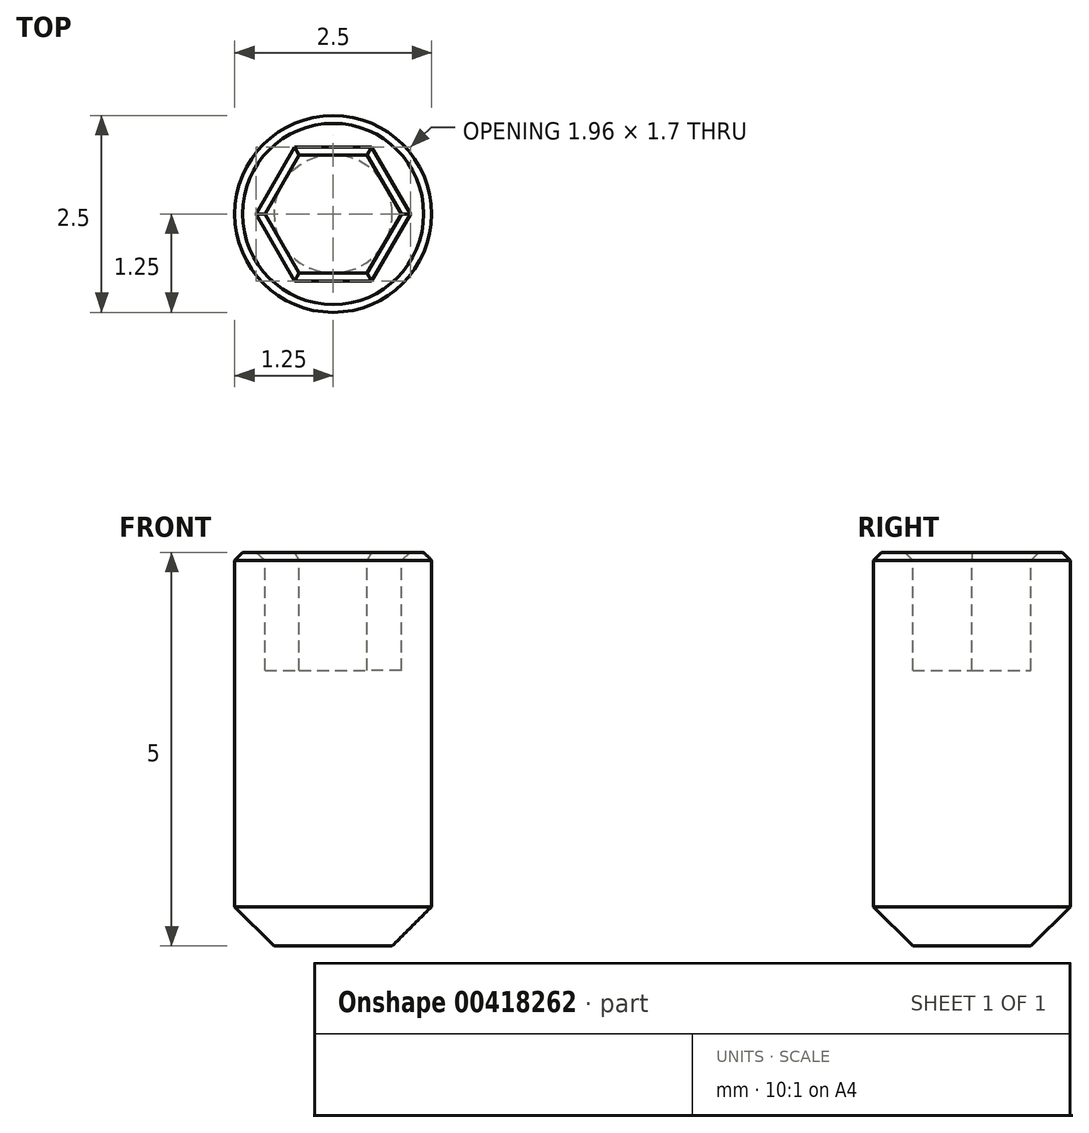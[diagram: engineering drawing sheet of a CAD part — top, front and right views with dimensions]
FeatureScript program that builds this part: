
annotation { "Feature Type Name" : "Feature", "Feature Type Description" : "" }
export const myFeature = defineFeature(function(context is Context, id is Id, definition is map)
    precondition{}
    {
        {
            var Q0;
            Q0=qCreatedBy(makeId("Top.planeOp"),FACE);
            var sketch = newSketch(context, id + "F0", { "sketchPlane" : qUnion([Q0])});
            skCircle(sketch, "E0", {"center": v(0, 0) * mm, "radius": 1.25 * mm});
            skCircle(sketch, "E1.cCircle", {"center": v(0, 0) * mm, "radius": 0.75 * mm, "construction": true});
            skLineSegment(sketch, "E1.0", {"start": v(-0.43, 0.75) * mm, "end": v(0.43, 0.75) * mm});
            skLineSegment(sketch, "E1.1", {"start": v(0.43, 0.75) * mm, "end": v(0.87, 0) * mm});
            skLineSegment(sketch, "E1.2", {"start": v(0.87, 0) * mm, "end": v(0.43, -0.75) * mm});
            skLineSegment(sketch, "E1.3", {"start": v(0.43, -0.75) * mm, "end": v(-0.43, -0.75) * mm});
            skLineSegment(sketch, "E1.4", {"start": v(-0.43, -0.75) * mm, "end": v(-0.87, 0) * mm});
            skLineSegment(sketch, "E1.5", {"start": v(-0.87, 0) * mm, "end": v(-0.43, 0.75) * mm});
            skPoint(sketch, "E1.0.midPoint", {"position": v(0, 0.75) * mm});
            skSolve(sketch);
        }
        {
            var Q0;
            Q0=makeQuery(id+"F0.imprint","IMPRINT",FACE,{"disambiguationData":[TD([[makeQuery(id+"F0.imprint","IMPRINT",EDGE,{"derivedFrom":sQuery(id+"F0.wireOp",EDGE,"E0")}),1.0]])]});
            var Q1;
            Q1=makeQuery(id+"F0.imprint","IMPRINT",FACE,{"disambiguationData":[TD([[makeQuery(id+"F0.imprint","IMPRINT",EDGE,{"derivedFrom":sQuery(id+"F0.wireOp",EDGE,"E1.0")}),-1.0]])]});
            extrude(context, id + "F1", {"entities" : qUnion([Q0, Q1]), "oppositeDirection" : true, "depth" : 5 * mm});
        }
        {
            var Q0;
            Q0=makeQuery(id+"F0.imprint","IMPRINT",FACE,{"disambiguationData":[TD([[makeQuery(id+"F0.imprint","IMPRINT",EDGE,{"derivedFrom":sQuery(id+"F0.wireOp",EDGE,"E1.0")}),-1.0]])]});
            extrude(context, id + "F2", {"entities" : qUnion([Q0]), "operationType" : NewBodyOperationType.REMOVE, "oppositeDirection" : true, "depth" : 1.5 * mm});
        }
        {
            var Q0;
            Q0=makeQuery(id+"F1.opExtrude","CAP_FACE",FACE,{"disambiguationData":[OSD([sQuery(id+"F0.wireOp",EDGE,"E0"),sQuery(id+"F0.wireOp",EDGE,"E1.0"),sQuery(id+"F0.wireOp",EDGE,"E1.1"),sQuery(id+"F0.wireOp",EDGE,"E1.2"),sQuery(id+"F0.wireOp",EDGE,"E1.3"),sQuery(id+"F0.wireOp",EDGE,"E1.4"),sQuery(id+"F0.wireOp",EDGE,"E1.5")])],"isStart":true});
            chamfer(context, id + "F3", {"entities" : qUnion([Q0]), "width" : 0.1 * mm, "tangentPropagation" : true});
        }
        {
            var Q0;
            Q0=makeQuery(id+"F1.opExtrude","CAP_EDGE",EDGE,{"disambiguationData":[OSD([sQuery(id+"F0.wireOp",EDGE,"E0")])],"isStart":false});
            chamfer(context, id + "F4", {"entities" : qUnion([Q0]), "width" : 0.5 * mm, "tangentPropagation" : true});
        }
    });
